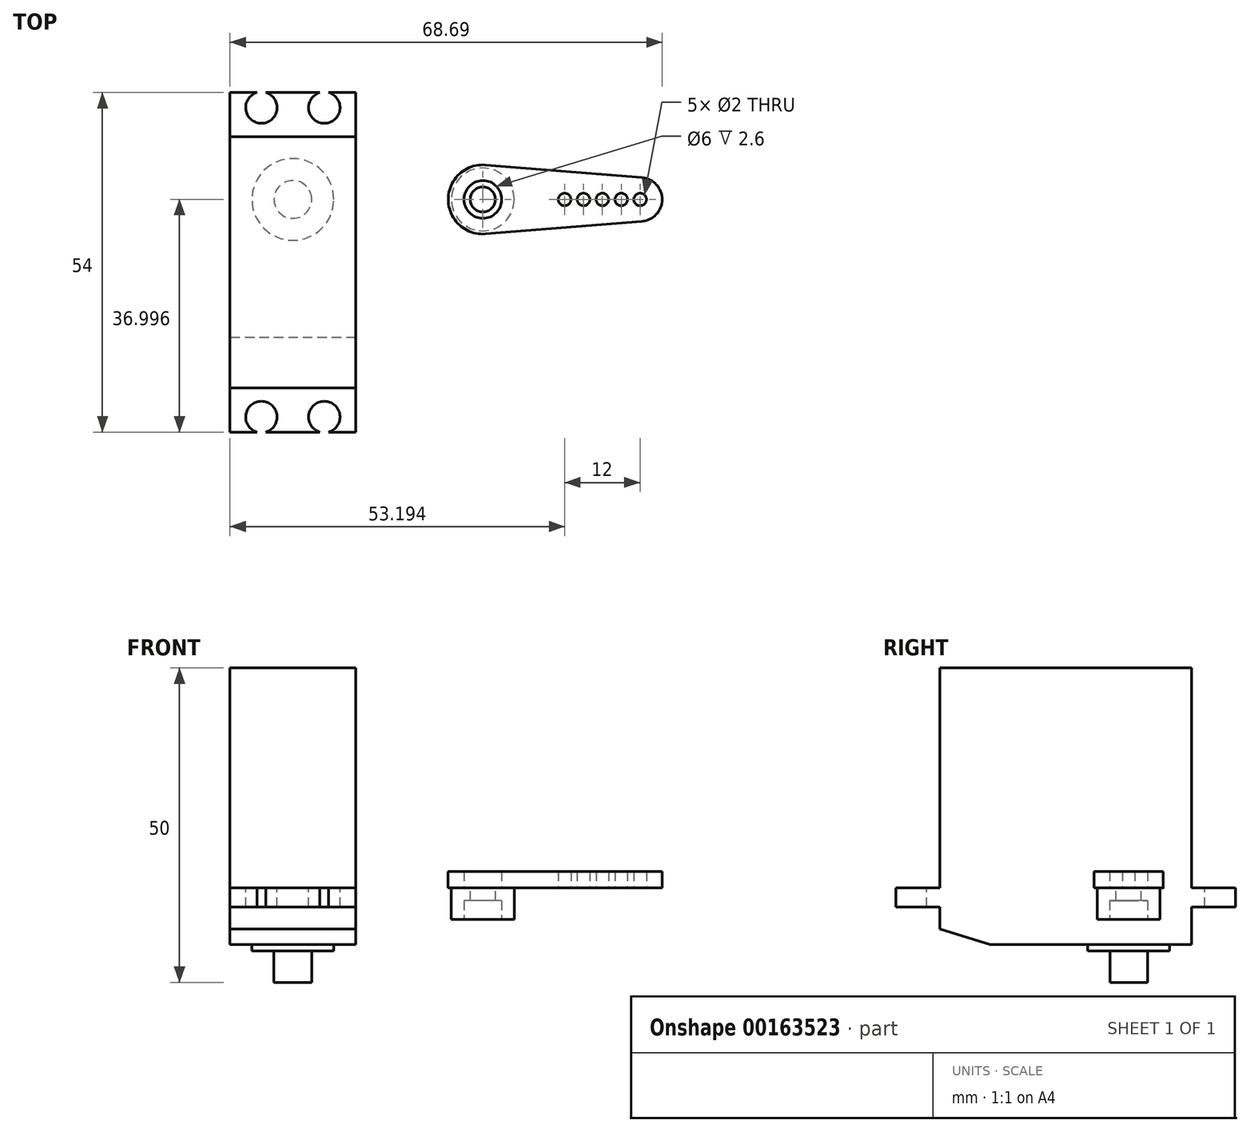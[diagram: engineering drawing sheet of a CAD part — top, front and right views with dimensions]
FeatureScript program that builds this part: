
annotation { "Feature Type Name" : "Feature", "Feature Type Description" : "" }
export const myFeature = defineFeature(function(context is Context, id is Id, definition is map)
    precondition{}
    {
        {
            var Q0;
            Q0=qCreatedBy(makeId("Top.planeOp"),FACE);
            var sketch = newSketch(context, id + "F0", { "sketchPlane" : qUnion([Q0])});
            skLineSegment(sketch, "E0.bottom", {"start": v(-10, 20) * mm, "end": v(10, 20) * mm});
            skLineSegment(sketch, "E0.top", {"start": v(-10, -20) * mm, "end": v(10, -20) * mm});
            skLineSegment(sketch, "E0.left", {"start": v(-10, 20) * mm, "end": v(-10, -20) * mm});
            skLineSegment(sketch, "E0.right", {"start": v(10, 20) * mm, "end": v(10, -20) * mm});
            skPoint(sketch, "E0.middle", {"position": v(0, 0) * mm});
            skLineSegment(sketch, "E1.0", {"start": v(-10, 27) * mm, "end": v(10, 27) * mm});
            skLineSegment(sketch, "E2.0", {"start": v(-10, -27) * mm, "end": v(10, -27) * mm});
            skLineSegment(sketch, "E3", {"start": v(-10, 27) * mm, "end": v(-10, 20) * mm});
            skLineSegment(sketch, "E4", {"start": v(10, 27) * mm, "end": v(10, 20) * mm});
            skLineSegment(sketch, "E5", {"start": v(10, -20) * mm, "end": v(10, -27) * mm});
            skLineSegment(sketch, "E6", {"start": v(-10, -20) * mm, "end": v(-10, -27) * mm});
            skLineSegment(sketch, "E7.0", {"start": v(-5, 27) * mm, "end": v(-5, -27) * mm, "construction": true});
            skLineSegment(sketch, "E8.0", {"start": v(5, 27) * mm, "end": v(5, -27) * mm, "construction": true});
            skLineSegment(sketch, "E9", {"start": v(-10, 24.6) * mm, "end": v(10, 24.6) * mm, "construction": true});
            skLineSegment(sketch, "E10", {"start": v(-10, -24.6) * mm, "end": v(10, -24.6) * mm, "construction": true});
            skCircle(sketch, "E11", {"center": v(-5, 24.6) * mm, "radius": 2.5 * mm});
            skCircle(sketch, "E12", {"center": v(-5, -24.6) * mm, "radius": 2.5 * mm});
            skCircle(sketch, "E13", {"center": v(5, 24.6) * mm, "radius": 2.5 * mm});
            skCircle(sketch, "E14", {"center": v(5, -24.6) * mm, "radius": 2.5 * mm});
            skLineSegment(sketch, "E15.0", {"start": v(-10, 10) * mm, "end": v(10, 10) * mm, "construction": true});
            skCircle(sketch, "E16", {"center": v(0, 10) * mm, "radius": 3 * mm});
            skCircle(sketch, "E17", {"center": v(0, 10) * mm, "radius": 6.5 * mm});
            skCircle(sketch, "E18", {"center": v(30.2, 10) * mm, "radius": 3 * mm});
            skArc(sketch, "E19", {"start": v(30.63, 15.48) * mm, "mid": v(24.7, 10) * mm, "end": v(30.63, 4.51) * mm});
            skCircle(sketch, "E20", {"center": v(30.2, 10) * mm, "radius": 5 * mm});
            skPoint(sketch, "E21", {"position": v(55.2, 10) * mm});
            skCircle(sketch, "E22", {"center": v(55.2, 10) * mm, "radius": 1 * mm});
            skLineSegment(sketch, "E23", {"start": v(30.63, 15.48) * mm, "end": v(55.47, 13.48) * mm});
            skLineSegment(sketch, "E24", {"start": v(30.63, 4.51) * mm, "end": v(55.47, 6.5) * mm});
            skCircle(sketch, "E25.1.0.0", {"center": v(52.2, 10) * mm, "radius": 1 * mm});
            skCircle(sketch, "E25.2.0.0", {"center": v(49.2, 10) * mm, "radius": 1 * mm});
            skCircle(sketch, "E25.3.0.0", {"center": v(46.2, 10) * mm, "radius": 1 * mm});
            skCircle(sketch, "E25.4.0.0", {"center": v(43.2, 10) * mm, "radius": 1 * mm});
            skLineSegment(sketch, "E25.direction1", {"start": v(55.2, 10) * mm, "end": v(52.2, 10) * mm, "construction": true});
            skArc(sketch, "E26.trimOffspring", {"start": v(55.47, 6.5) * mm, "mid": v(58.7, 10) * mm, "end": v(55.47, 13.48) * mm});
            skCircle(sketch, "E27", {"center": v(30.2, 10) * mm, "radius": 2 * mm});
            skSolve(sketch);
        }
        {
            var Q0;
            Q0=makeQuery(id+"F0.imprint","IMPRINT",FACE,{"disambiguationData":[TD([[makeQuery(id+"F0.imprint","IMPRINT",EDGE,{"derivedFrom":sQuery(id+"F0.wireOp",EDGE,"E0.bottom")}),-1.0]])]});
            var Q1;
            Q1=makeQuery(id+"F0.imprint","IMPRINT",FACE,{"disambiguationData":[TD([[makeQuery(id+"F0.imprint","IMPRINT",EDGE,{"derivedFrom":sQuery(id+"F0.wireOp",EDGE,"E16")}),-1.0]])]});
            var Q2;
            Q2=makeQuery(id+"F0.imprint","IMPRINT",FACE,{"disambiguationData":[TD([[makeQuery(id+"F0.imprint","IMPRINT",EDGE,{"derivedFrom":sQuery(id+"F0.wireOp",EDGE,"E16")}),1.0]])]});
            extrude(context, id + "F1", {"entities" : qUnion([Q0, Q1, Q2]), "depth" : 35 * mm});
        }
        {
            var Q0;
            Q0=makeQuery(id+"F0.imprint","IMPRINT",FACE,{"disambiguationData":[TD([[makeQuery(id+"F0.imprint","IMPRINT",EDGE,{"derivedFrom":sQuery(id+"F0.wireOp",EDGE,"E0.bottom")}),-1.0]])]});
            var Q1;
            Q1=makeQuery(id+"F0.imprint","IMPRINT",FACE,{"disambiguationData":[TD([[makeQuery(id+"F0.imprint","IMPRINT",EDGE,{"derivedFrom":sQuery(id+"F0.wireOp",EDGE,"E16")}),1.0]])]});
            var Q2;
            Q2=makeQuery(id+"F0.imprint","IMPRINT",FACE,{"disambiguationData":[TD([[makeQuery(id+"F0.imprint","IMPRINT",EDGE,{"derivedFrom":sQuery(id+"F0.wireOp",EDGE,"E16")}),-1.0]])]});
            extrude(context, id + "F2", {"entities" : qUnion([Q0, Q1, Q2]), "operationType" : NewBodyOperationType.ADD, "oppositeDirection" : true, "depth" : 9 * mm});
        }
        {
            var Q0;
            Q0=makeQuery(id+"F0.imprint","IMPRINT",FACE,{"disambiguationData":[TD([[makeQuery(id+"F0.imprint","IMPRINT",EDGE,{"derivedFrom":sQuery(id+"F0.wireOp",EDGE,"E0.bottom")}),1.0]])]});
            var Q1;
            Q1=makeQuery(id+"F0.imprint","IMPRINT",FACE,{"disambiguationData":[TD([[makeQuery(id+"F0.imprint","IMPRINT",EDGE,{"derivedFrom":sQuery(id+"F0.wireOp",EDGE,"E0.top")}),-1.0]])]});
            var Q2;
            Q2=makeQuery(id+"F0.imprint","IMPRINT",FACE,{"disambiguationData":[TD([[makeQuery(id+"F0.imprint","IMPRINT",EDGE,{"derivedFrom":sQuery(id+"F0.wireOp",EDGE,"E0.bottom")}),-1.0]])]});
            var Q3;
            Q3=makeQuery(id+"F0.imprint","IMPRINT",FACE,{"disambiguationData":[TD([[makeQuery(id+"F0.imprint","IMPRINT",EDGE,{"derivedFrom":sQuery(id+"F0.wireOp",EDGE,"E16")}),-1.0]])]});
            var Q4;
            Q4=makeQuery(id+"F0.imprint","IMPRINT",FACE,{"disambiguationData":[TD([[makeQuery(id+"F0.imprint","IMPRINT",EDGE,{"derivedFrom":sQuery(id+"F0.wireOp",EDGE,"E16")}),1.0]])]});
            extrude(context, id + "F3", {"entities" : qUnion([Q0, Q1, Q2, Q3, Q4]), "operationType" : NewBodyOperationType.ADD, "oppositeDirection" : true, "depth" : 3 * mm});
        }
        {
            var Q0;
            Q0=makeQuery(id+"F2.opExtrude","CAP_EDGE",EDGE,{"disambiguationData":[OSD([sQuery(id+"F0.wireOp",EDGE,"E0.top")])],"isStart":false});
            chamfer(context, id + "F4", {"entities" : qUnion([Q0]), "chamferType" : ChamferType.TWO_OFFSETS, "width1" : 2.5 * mm, "oppositeDirection" : false, "width2" : 8 * mm, "tangentPropagation" : true});
        }
        {
            var Q0;
            Q0=makeQuery(id+"F0.imprint","IMPRINT",FACE,{"disambiguationData":[TD([[makeQuery(id+"F0.imprint","IMPRINT",EDGE,{"derivedFrom":sQuery(id+"F0.wireOp",EDGE,"E16")}),-1.0]])]});
            extrude(context, id + "F5", {"entities" : qUnion([Q0]), "operationType" : NewBodyOperationType.ADD, "oppositeDirection" : true, "depth" : 10 * mm});
        }
        {
            var Q0;
            Q0=makeQuery(id+"F0.imprint","IMPRINT",FACE,{"disambiguationData":[TD([[makeQuery(id+"F0.imprint","IMPRINT",EDGE,{"derivedFrom":sQuery(id+"F0.wireOp",EDGE,"E16")}),1.0]])]});
            extrude(context, id + "F6", {"entities" : qUnion([Q0]), "operationType" : NewBodyOperationType.ADD, "oppositeDirection" : true, "depth" : 15 * mm});
        }
        {
            var Q0;
            Q0=makeQuery(id+"F0.imprint","IMPRINT",FACE,{"disambiguationData":[TD([[makeQuery(id+"F0.imprint","IMPRINT",EDGE,{"derivedFrom":sQuery(id+"F0.wireOp",EDGE,"E19")}),1.0]])]});
            var Q1;
            Q1=makeQuery(id+"F0.imprint","IMPRINT",FACE,{"disambiguationData":[TD([[makeQuery(id+"F0.imprint","IMPRINT",EDGE,{"derivedFrom":sQuery(id+"F0.wireOp",EDGE,"E18")}),-1.0]])]});
            extrude(context, id + "F7", {"entities" : qUnion([Q0, Q1]), "depth" : 2.6 * mm});
        }
        {
            var Q0;
            Q0=makeQuery(id+"F0.imprint","IMPRINT",FACE,{"disambiguationData":[TD([[makeQuery(id+"F0.imprint","IMPRINT",EDGE,{"derivedFrom":sQuery(id+"F0.wireOp",EDGE,"E18")}),-1.0]])]});
            extrude(context, id + "F8", {"entities" : qUnion([Q0]), "operationType" : NewBodyOperationType.ADD, "oppositeDirection" : true, "depth" : 5 * mm});
        }
        {
            var Q0;
            Q0=makeQuery(id+"F0.imprint","IMPRINT",FACE,{"disambiguationData":[TD([[makeQuery(id+"F0.imprint","IMPRINT",EDGE,{"derivedFrom":sQuery(id+"F0.wireOp",EDGE,"E18")}),1.0]])]});
            extrude(context, id + "F9", {"entities" : qUnion([Q0]), "operationType" : NewBodyOperationType.ADD, "oppositeDirection" : true, "depth" : 2 * mm});
        }
    });
